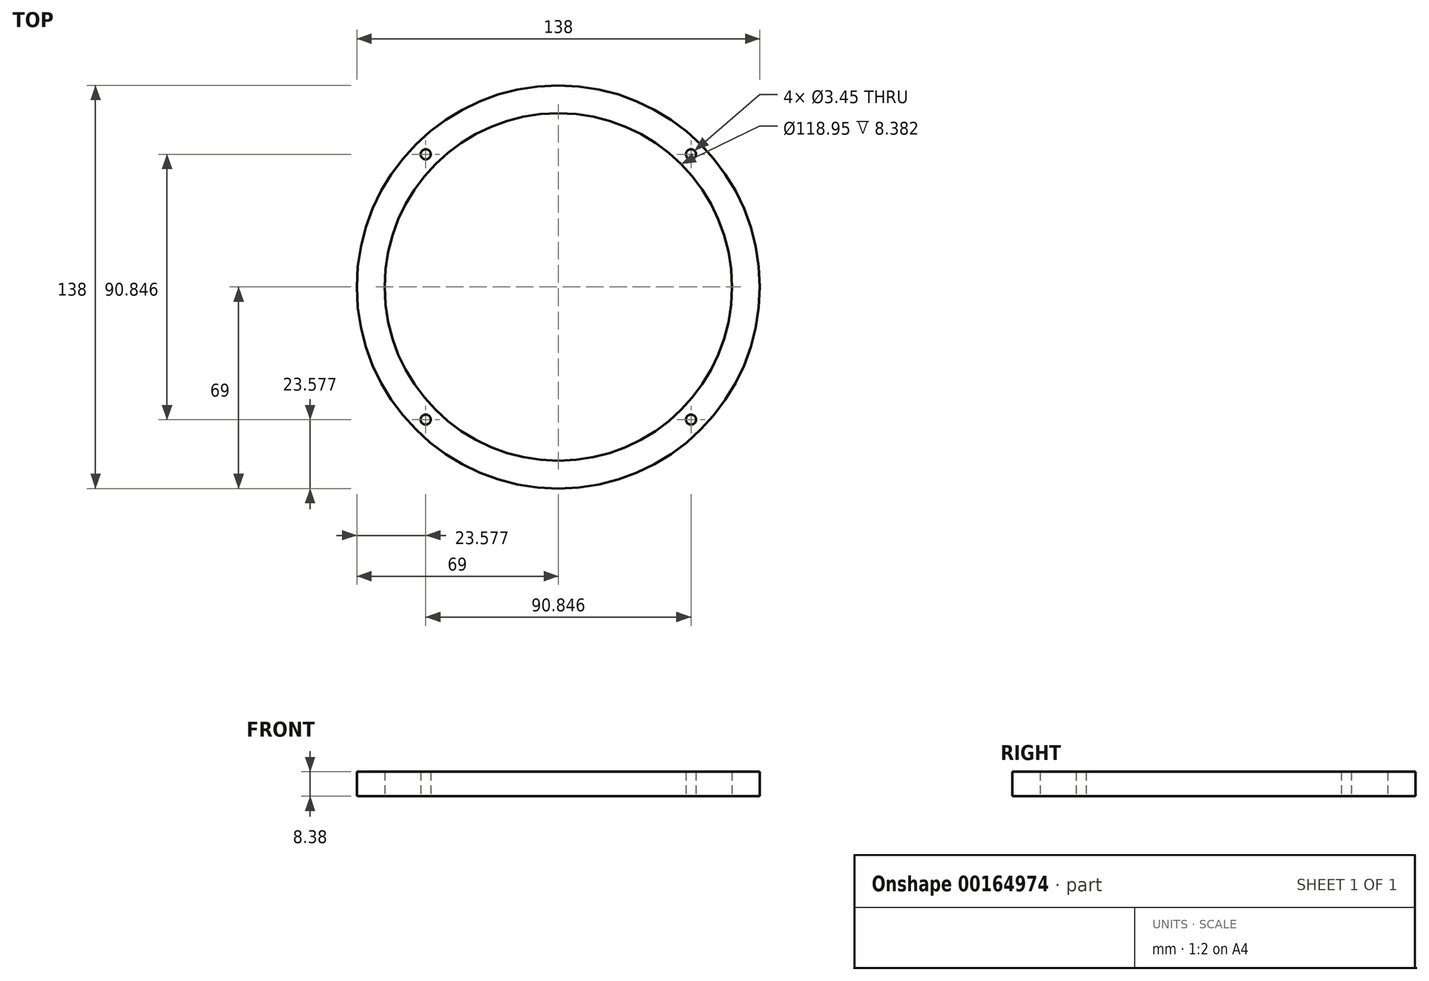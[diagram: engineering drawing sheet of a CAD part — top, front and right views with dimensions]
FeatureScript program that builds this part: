
annotation { "Feature Type Name" : "Feature", "Feature Type Description" : "" }
export const myFeature = defineFeature(function(context is Context, id is Id, definition is map)
    precondition{}
    {
        {
            var Q0;
            Q0=qCreatedBy(makeId("Top.planeOp"),FACE);
            var sketch = newSketch(context, id + "F0", { "sketchPlane" : qUnion([Q0])});
            skCircle(sketch, "E0", {"center": v(0, 0) * mm, "radius": 59.47 * mm});
            skCircle(sketch, "E1", {"center": v(0, 0) * mm, "radius": 69 * mm});
            skLineSegment(sketch, "E2.bottom", {"start": v(45.42, 45.42) * mm, "end": v(-45.42, 45.42) * mm, "construction": true});
            skLineSegment(sketch, "E2.top", {"start": v(45.42, -45.42) * mm, "end": v(-45.42, -45.42) * mm, "construction": true});
            skLineSegment(sketch, "E2.left", {"start": v(45.42, 45.42) * mm, "end": v(45.42, -45.42) * mm, "construction": true});
            skLineSegment(sketch, "E2.right", {"start": v(-45.42, 45.42) * mm, "end": v(-45.42, -45.42) * mm, "construction": true});
            skCircle(sketch, "E3", {"center": v(-45.42, 45.42) * mm, "radius": 4.76 * mm, "construction": true});
            skCircle(sketch, "E4", {"center": v(-45.42, 45.42) * mm, "radius": 1.73 * mm});
            skCircle(sketch, "E5", {"center": v(45.42, 45.42) * mm, "radius": 1.73 * mm});
            skCircle(sketch, "E6", {"center": v(45.42, -45.42) * mm, "radius": 1.73 * mm});
            skCircle(sketch, "E7", {"center": v(-45.42, -45.42) * mm, "radius": 1.73 * mm});
            skSolve(sketch);
        }
        {
            var Q0;
            Q0 = qSketchRegion(id + "F0", true);
            extrude(context, id + "F1", {"entities" : qUnion([Q0]), "depth" : 8.38 * mm});
        }
    });
